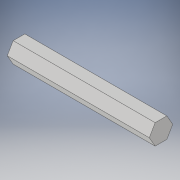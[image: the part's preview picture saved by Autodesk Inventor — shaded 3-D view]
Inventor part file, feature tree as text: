
AUTODESK INVENTOR PART (.ipt)
format: ipt  version: 2018 (Build 220112000, 112)  size: 94,208 bytes
history: native  units: in
note: dims shown in document units (in); Inventor stores cm internally (conversion verified against a paired STEP export)
features: extrude x1, sketch x1
ambient origin geometry x8: Origin, YZ Plane, XZ Plane, XY Plane, X Axis, Y Axis, Z Axis, Center Point
bodies: Solid1 (feature_tree)
feature tree (2):
  extrude  "Extrusion1"  Depth=3.5in TaperAngle=0.0deg
  sketch  "Sketch1"  dims[d0=0.25in d1=3.5in d2=0.0in]
